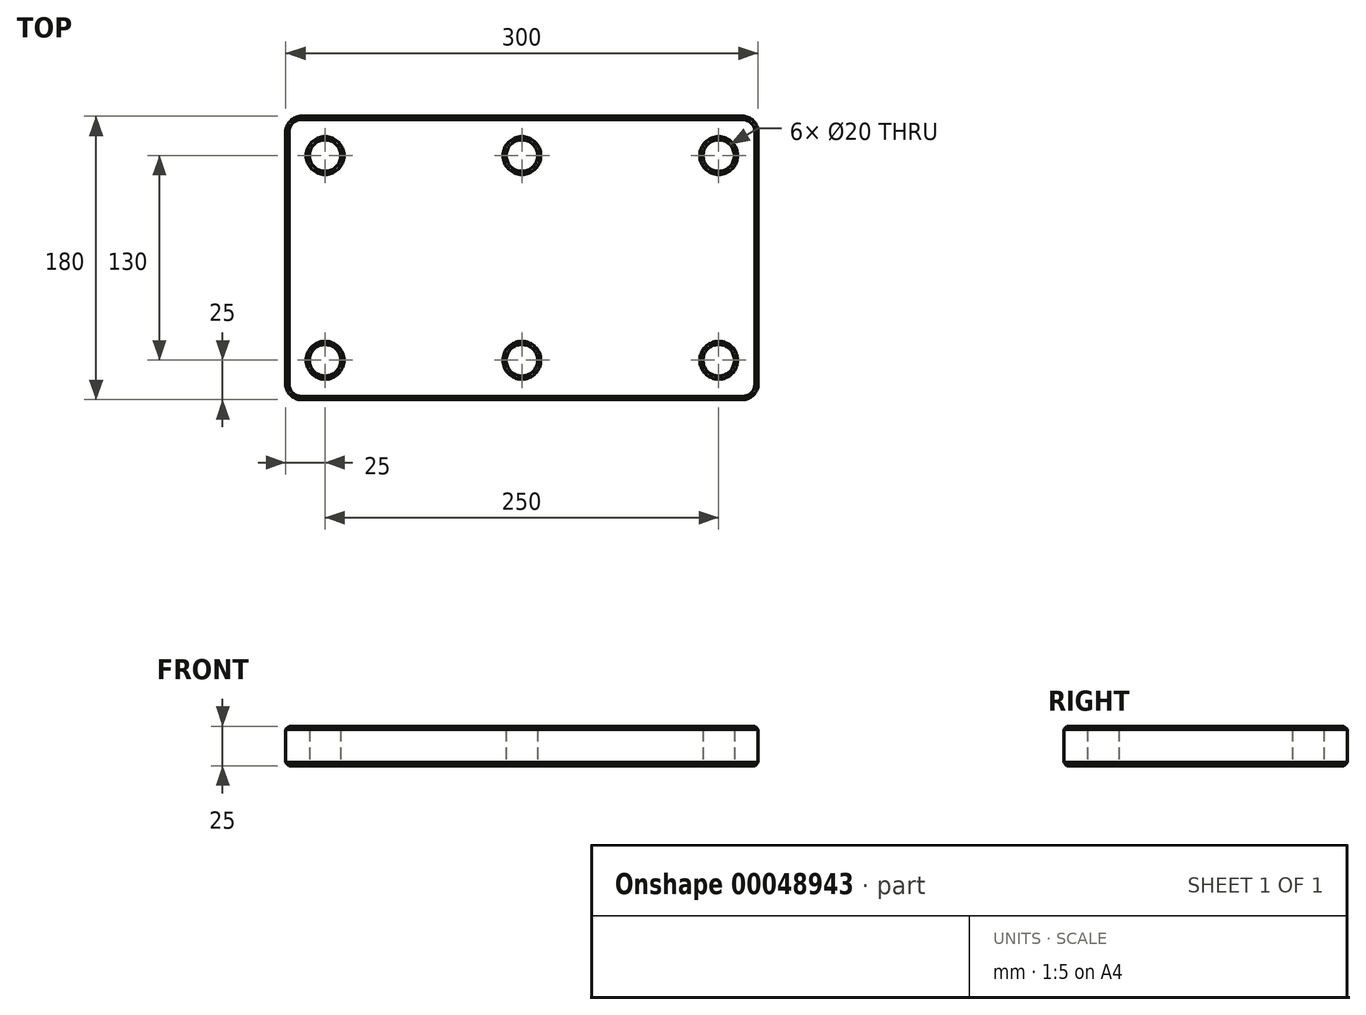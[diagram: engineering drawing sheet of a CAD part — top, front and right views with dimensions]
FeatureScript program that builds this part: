
annotation { "Feature Type Name" : "Feature", "Feature Type Description" : "" }
export const myFeature = defineFeature(function(context is Context, id is Id, definition is map)
    precondition{}
    {
        {
            var Q0;
            Q0=qCreatedBy(makeId("Top.planeOp"),FACE);
            var sketch = newSketch(context, id + "F0", { "sketchPlane" : qUnion([Q0])});
            skLineSegment(sketch, "E0.rect.bottom", {"start": v(150, 90) * mm, "end": v(-150, 90) * mm});
            skLineSegment(sketch, "E0.rect.top", {"start": v(150, -90) * mm, "end": v(-150, -90) * mm});
            skLineSegment(sketch, "E0.rect.left", {"start": v(150, 90) * mm, "end": v(150, -90) * mm});
            skLineSegment(sketch, "E0.rect.right", {"start": v(-150, 90) * mm, "end": v(-150, -90) * mm});
            skPoint(sketch, "E0.rect.middle", {"position": v(0, 0) * mm});
            skLineSegment(sketch, "E1.rect.bottom", {"start": v(125, -65) * mm, "end": v(-125, -65) * mm, "construction": true});
            skLineSegment(sketch, "E1.rect.top", {"start": v(125, 65) * mm, "end": v(-125, 65) * mm, "construction": true});
            skLineSegment(sketch, "E1.rect.left", {"start": v(125, -65) * mm, "end": v(125, 65) * mm, "construction": true});
            skLineSegment(sketch, "E1.rect.right", {"start": v(-125, -65) * mm, "end": v(-125, 65) * mm, "construction": true});
            skLineSegment(sketch, "E2", {"start": v(0, -65) * mm, "end": v(0, 65) * mm, "construction": true});
            skCircle(sketch, "E3", {"center": v(-125, 65) * mm, "radius": 10 * mm});
            skCircle(sketch, "E4", {"center": v(0, 65) * mm, "radius": 10 * mm});
            skCircle(sketch, "E5", {"center": v(125, 65) * mm, "radius": 10 * mm});
            skCircle(sketch, "E6", {"center": v(125, -65) * mm, "radius": 10 * mm});
            skCircle(sketch, "E7", {"center": v(0, -65) * mm, "radius": 10 * mm});
            skCircle(sketch, "E8", {"center": v(-125, -65) * mm, "radius": 10 * mm});
            skSolve(sketch);
        }
        {
            var Q0;
            Q0=makeQuery(id+"F0.imprint","IMPRINT",FACE,{"disambiguationData":[TD([[makeQuery(id+"F0.imprint","IMPRINT",EDGE,{"derivedFrom":sQuery(id+"F0.wireOp",EDGE,"E0.rect.bottom")}),1.0]])]});
            extrude(context, id + "F1", {"entities" : qUnion([Q0]), "depth" : 25 * mm});
        }
        {
            var Q0;
            Q0=makeQuery(id+"F1.opExtrude","SWEPT_EDGE",EDGE,{"disambiguationData":[OSD([sQuery(id+"F0.wireOp",EDGE,"E0.rect.top"),sQuery(id+"F0.wireOp",EDGE,"E0.rect.right")])]});
            var Q1;
            Q1=makeQuery(id+"F1.opExtrude","SWEPT_EDGE",EDGE,{"disambiguationData":[OSD([sQuery(id+"F0.wireOp",EDGE,"E0.rect.bottom"),sQuery(id+"F0.wireOp",EDGE,"E0.rect.right")])]});
            var Q2;
            Q2=makeQuery(id+"F1.opExtrude","SWEPT_EDGE",EDGE,{"disambiguationData":[OSD([sQuery(id+"F0.wireOp",EDGE,"E0.rect.top"),sQuery(id+"F0.wireOp",EDGE,"E0.rect.left")])]});
            var Q3;
            Q3=makeQuery(id+"F1.opExtrude","SWEPT_EDGE",EDGE,{"disambiguationData":[OSD([sQuery(id+"F0.wireOp",EDGE,"E0.rect.bottom"),sQuery(id+"F0.wireOp",EDGE,"E0.rect.left")])]});
            fillet(context, id + "F2", {"entities" : qUnion([Q0, Q1, Q2, Q3]), "radius" : 10 * mm, "tangentPropagation" : true, "allowEdgeOverflow" : false});
        }
        {
            var Q0;
            Q0=makeQuery(id+"F1.opExtrude","CAP_FACE",FACE,{"disambiguationData":[OSD([sQuery(id+"F0.wireOp",EDGE,"E0.rect.bottom"),sQuery(id+"F0.wireOp",EDGE,"E0.rect.top"),sQuery(id+"F0.wireOp",EDGE,"E0.rect.left"),sQuery(id+"F0.wireOp",EDGE,"E0.rect.right"),sQuery(id+"F0.wireOp",EDGE,"E3"),sQuery(id+"F0.wireOp",EDGE,"E4"),sQuery(id+"F0.wireOp",EDGE,"E5"),sQuery(id+"F0.wireOp",EDGE,"E6"),sQuery(id+"F0.wireOp",EDGE,"E7"),sQuery(id+"F0.wireOp",EDGE,"E8")])],"isStart":false});
            var Q1;
            Q1=makeQuery(id+"F1.opExtrude","CAP_FACE",FACE,{"disambiguationData":[OSD([sQuery(id+"F0.wireOp",EDGE,"E0.rect.bottom"),sQuery(id+"F0.wireOp",EDGE,"E0.rect.top"),sQuery(id+"F0.wireOp",EDGE,"E0.rect.left"),sQuery(id+"F0.wireOp",EDGE,"E0.rect.right"),sQuery(id+"F0.wireOp",EDGE,"E3"),sQuery(id+"F0.wireOp",EDGE,"E4"),sQuery(id+"F0.wireOp",EDGE,"E5"),sQuery(id+"F0.wireOp",EDGE,"E6"),sQuery(id+"F0.wireOp",EDGE,"E7"),sQuery(id+"F0.wireOp",EDGE,"E8")])],"isStart":true});
            chamfer(context, id + "F3", {"entities" : qUnion([Q0, Q1]), "chamferType" : ChamferType.OFFSET_ANGLE, "width" : 2 * mm, "oppositeDirection" : false, "angle" : 45 * degree, "tangentPropagation" : true});
        }
    });
